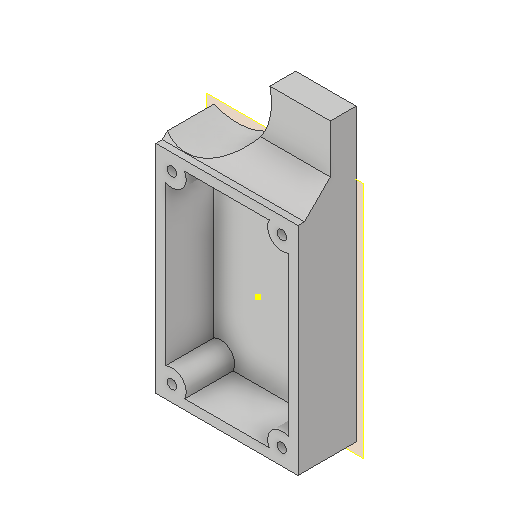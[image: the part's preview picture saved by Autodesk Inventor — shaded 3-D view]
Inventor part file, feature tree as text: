
AUTODESK INVENTOR PART (.ipt)
format: ipt  version: 2022 (Build 260153000, 153)  size: 178,688 bytes
history: native  units: mm
features: sketch x4, reference x4, other x4, extrude x2, plane x1, chamfer x1, shell x1, hole x1, projected_geometry x1
ambient origin geometry x8: Origin, YZ Plane, XZ Plane, XY Plane, X Axis, Y Axis, Z Axis, Center Point
bodies: Solid1 (feature_tree)
feature tree (19):
  sketch  "Sketch1"  dims[d0=-18.0mm d1=90.0mm]
  plane  "Work Plane1"
  sketch  "Sketch2"  dims[d2=10.0mm d3=0.0mm d4=10.0mm d5=0.0mm d6=8.0mm d7=2.0mm d8=45.0deg d9=3.0mm]
  extrude  "Extrusion1"  Depth=90.0mm
  extrude  "Extrusion2"  Depth=10.0mm TaperAngle=0.0deg
  chamfer  "Chamfer1"  Distance=8.0mm Angle=45.0deg
  sketch  "Sketch3"  dims[d10=2.9mm d11=6.0mm d12=7.0mm d13=4.0mm d14=90.0deg d15=15.0mm d16=20.594885mm]
  shell  "Shell1"  Thickness=3.0mm
  hole  "Hole1"  [1 undecoded]
  reference  "Reference1"
  reference  "Reference2"
  reference  "Reference3"
  reference  "Reference4"
  sketch  "Sketch4"
  projected_geometry  "Projected Loop1"
  other  "<userpath>\Documents\GitHub\cellstorm\INVENTOR\cellSTORM_v6.iam"
  other  "cellSTORM_v6.iam"
  other  "cellSTORM_v5_cellphonestage:1"
  other  "cellSTORM_v5_microsocpe:1"
note: 1 required parameter value undecoded (feature->parameter linkage not recoverable at this tier; creation-order binding heuristic only, values carry confidence <= 0.55)
